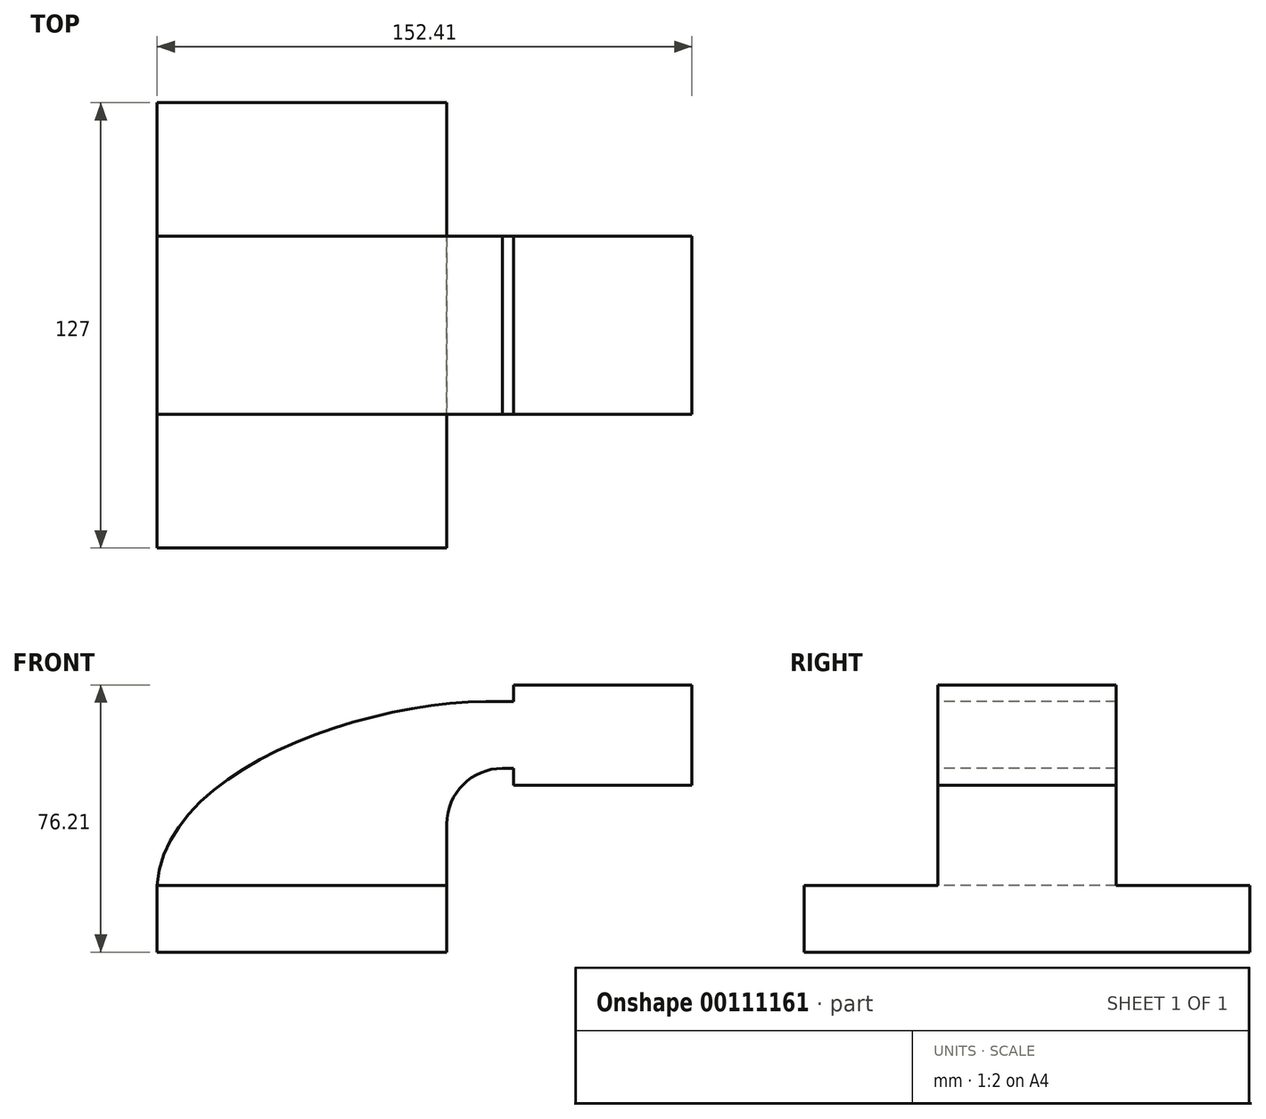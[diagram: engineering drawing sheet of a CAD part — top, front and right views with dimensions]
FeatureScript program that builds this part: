
annotation { "Feature Type Name" : "Feature", "Feature Type Description" : "" }
export const myFeature = defineFeature(function(context is Context, id is Id, definition is map)
    precondition{}
    {
        {
            var Q0;
            Q0=qCreatedBy(makeId("Front.planeOp"),FACE);
            var sketch = newSketch(context, id + "F0", { "sketchPlane" : qUnion([Q0])});
            skLineSegment(sketch, "E0.bottom", {"start": v(41.28, 9.53) * mm, "end": v(-41.28, 9.52) * mm});
            skLineSegment(sketch, "E0.top", {"start": v(41.28, -9.52) * mm, "end": v(-41.28, -9.53) * mm});
            skLineSegment(sketch, "E0.left", {"start": v(41.28, 9.53) * mm, "end": v(41.28, -9.52) * mm});
            skLineSegment(sketch, "E0.right", {"start": v(-41.28, 9.52) * mm, "end": v(-41.28, -9.53) * mm});
            skPoint(sketch, "E0.middle", {"position": v(0, 0) * mm});
            skLineSegment(sketch, "E1", {"start": v(41.28, 9.53) * mm, "end": v(41.28, 27) * mm});
            skArc(sketch, "E2", {"start": v(41.27, 27) * mm, "mid": v(45.92, 38.23) * mm, "end": v(57.15, 42.88) * mm});
            skLineSegment(sketch, "E3.bottom", {"start": v(111.12, 66.68) * mm, "end": v(60.32, 66.68) * mm});
            skLineSegment(sketch, "E3.top", {"start": v(111.12, 38.1) * mm, "end": v(60.32, 38.1) * mm});
            skLineSegment(sketch, "E3.left", {"start": v(111.12, 38.1) * mm, "end": v(111.12, 66.68) * mm});
            skLineSegment(sketch, "E3.right", {"start": v(60.32, 38.1) * mm, "end": v(60.32, 66.68) * mm});
            skPoint(sketch, "E3.middle", {"position": v(85.72, 52.39) * mm});
            skLineSegment(sketch, "E4", {"start": v(57.15, 42.88) * mm, "end": v(85.73, 42.88) * mm});
            skLineSegment(sketch, "E5.0", {"start": v(57.15, 61.93) * mm, "end": v(85.73, 61.93) * mm});
            skArc(sketch, "E5.1", {"start": v(22.22, 27) * mm, "mid": v(32.45, 51.7) * mm, "end": v(57.15, 61.93) * mm});
            skLineSegment(sketch, "E5.2", {"start": v(22.22, 9.53) * mm, "end": v(22.22, 27) * mm});
            skLineSegment(sketch, "E6", {"start": v(85.73, 61.93) * mm, "end": v(85.73, 42.88) * mm});
            skFitSpline(sketch, "E7", {"points": [v(-41.28, 9.53) * mm, v(57.15, 61.93) * mm], "startDerivative": vector(7.75, 103.58) * mm, "endDerivative": vector(106.57, -3.7) * mm});
            skSolve(sketch);
        }
        {
            var Q0;
            Q0=makeQuery(id+"F0.imprint","IMPRINT",FACE,{"disambiguationData":[TD([[makeQuery(id+"F0.imprint","IMPRINT",EDGE,{"derivedFrom":sQuery(id+"F0.wireOp",EDGE,"E0.top")}),-1.0]])]});
            extrude(context, id + "F1", {"entities" : qUnion([Q0]), "endBound" : BoundingType.SYMMETRIC, "depth" : 127 * mm});
        }
        {
            var Q0;
            Q0 = qSketchRegion(id + "F0", true);
            extrude(context, id + "F2", {"entities" : qUnion([Q0]), "operationType" : NewBodyOperationType.ADD, "endBound" : BoundingType.SYMMETRIC, "oppositeDirection" : true, "depth" : 50.8 * mm});
        }
    });
